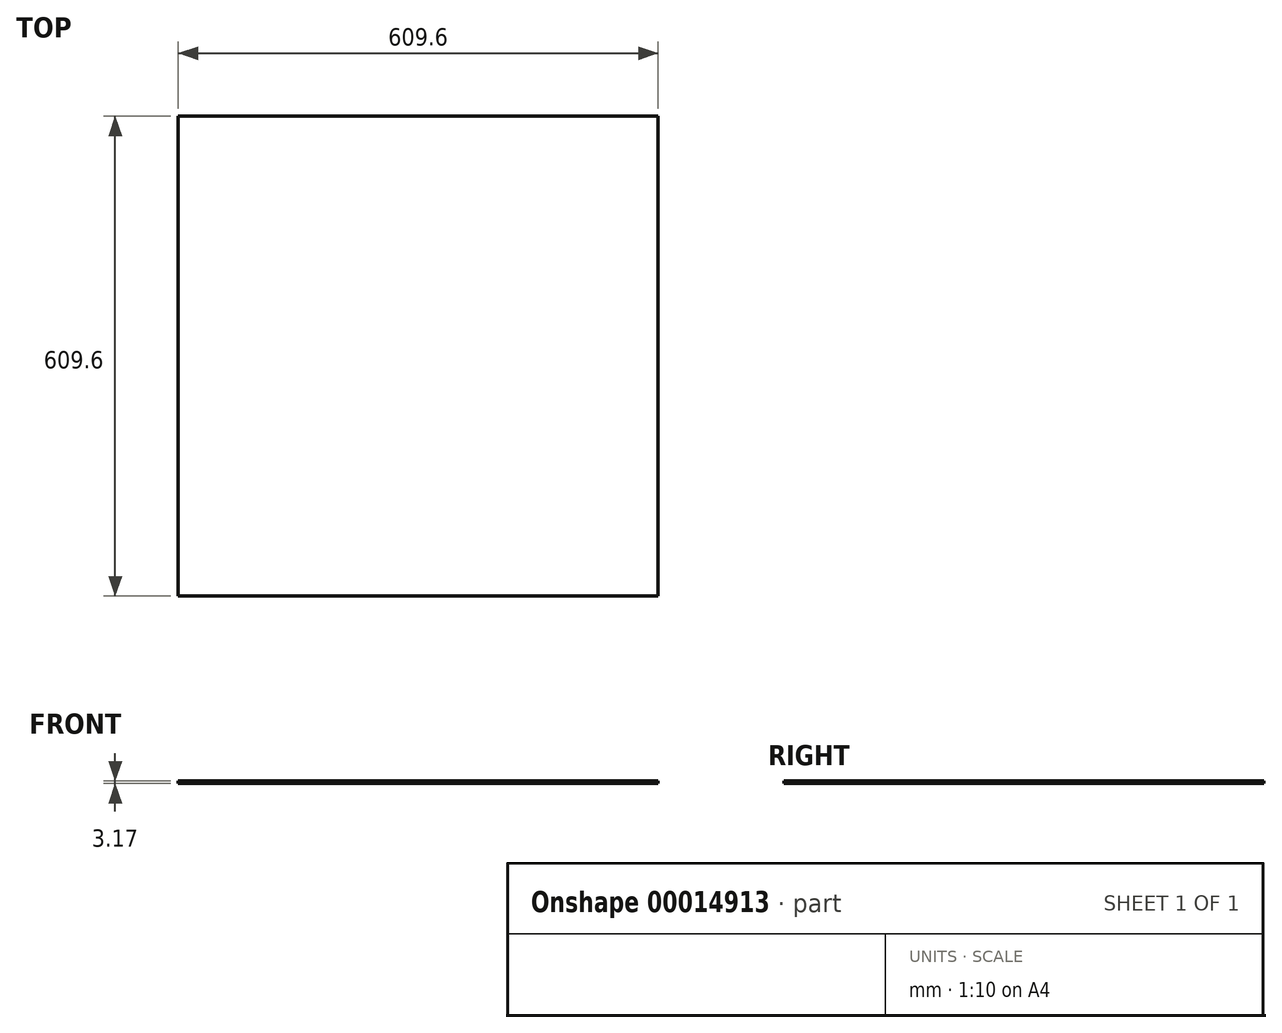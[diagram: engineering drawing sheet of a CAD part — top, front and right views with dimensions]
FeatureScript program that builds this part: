
annotation { "Feature Type Name" : "Feature", "Feature Type Description" : "" }
export const myFeature = defineFeature(function(context is Context, id is Id, definition is map)
    precondition{}
    {
        {
            var Q0;
            Q0=qCreatedBy(makeId("Top.planeOp"),FACE);
            var sketch = newSketch(context, id + "F0", { "sketchPlane" : qUnion([Q0])});
            skLineSegment(sketch, "E0.bottom", {"start": v(0, 0) * mm, "end": v(609.6, 0) * mm});
            skLineSegment(sketch, "E0.top", {"start": v(0, 609.6) * mm, "end": v(609.6, 609.6) * mm});
            skLineSegment(sketch, "E0.left", {"start": v(0, 0) * mm, "end": v(0, 609.6) * mm});
            skLineSegment(sketch, "E0.right", {"start": v(609.6, 0) * mm, "end": v(609.6, 609.6) * mm});
            skSolve(sketch);
        }
        {
            var Q0;
            Q0=makeQuery(id+"F0.imprint","IMPRINT",FACE,{"disambiguationData":[TD([[makeQuery(id+"F0.imprint","IMPRINT",EDGE,{"derivedFrom":sQuery(id+"F0.wireOp",EDGE,"E0.bottom")}),1.0]])]});
            extrude(context, id + "F1", {"entities" : qUnion([Q0]), "depth" : 3.17 * mm});
        }
    });
